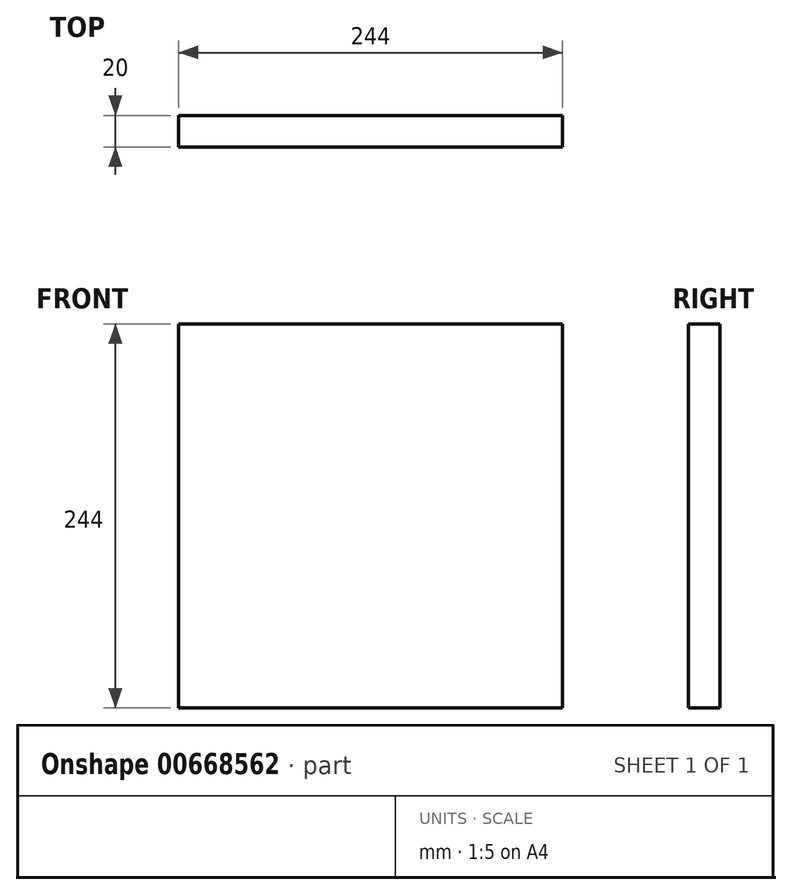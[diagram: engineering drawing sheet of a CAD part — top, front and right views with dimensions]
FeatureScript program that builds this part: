
annotation { "Feature Type Name" : "Feature", "Feature Type Description" : "" }
export const myFeature = defineFeature(function(context is Context, id is Id, definition is map)
    precondition{}
    {
        {
            var Q0;
            Q0=qCreatedBy(makeId("Front.planeOp"),FACE);
            var sketch = newSketch(context, id + "F0", { "sketchPlane" : qUnion([Q0])});
            skLineSegment(sketch, "E0.bottom", {"start": v(122, 122) * mm, "end": v(-122, 122) * mm});
            skLineSegment(sketch, "E0.top", {"start": v(122, -122) * mm, "end": v(-122, -122) * mm});
            skLineSegment(sketch, "E0.left", {"start": v(122, 122) * mm, "end": v(122, -122) * mm});
            skLineSegment(sketch, "E0.right", {"start": v(-122, 122) * mm, "end": v(-122, -122) * mm});
            skPoint(sketch, "E0.middle", {"position": v(0, 0) * mm});
            skSolve(sketch);
        }
        {
            var Q0;
            Q0=makeQuery(id+"F0.imprint","IMPRINT",FACE,{"disambiguationData":[TD([[makeQuery(id+"F0.imprint","IMPRINT",EDGE,{"derivedFrom":sQuery(id+"F0.wireOp",EDGE,"E0.bottom")}),1.0]])]});
            extrude(context, id + "F1", {"entities" : qUnion([Q0]), "depth" : 20 * mm, "offsetDistance" : 25 * mm});
        }
    });
